# Revit family: DFM Doors - double leaf door EI 120
name_source: partatom
category: Doors
revit_build: Autodesk Revit 2017 (Build: 20190507_1515(x64)
units: mm (PartAtom-declared; Revit-internal decimal feet)

## family parameters
Always vertical = Yes
Cut with Voids When Loaded = No
Host = Wall
OmniClass Number = 23.30.10.00
OmniClass Title = Doors
Room Calculation Point = Yes
Shared = No

## types (1)
- 2018x1840 internal frame
    Clear opening height = 2018 mm  [stored 6.62073 ft]
    Clear opening height. Limiting dimensions = ok
    Clear opening width = 1840 mm  [stored 6.03675 ft]
    Clear opening width at opened active leaf = 870.5 mm  [stored 2.85597 ft]
    Clear opening width. Limiting dimensions = ok
    Corner frame = No
    Embracing frame = No
    Fire Rating = EI 120
    Frame to frame width = 1851 mm  [stored 6.07283 ft]
    Function = Interior
    Height = 2101 mm  [stored 6.89304 ft]
    Height of the door leaf = 2050 mm  [stored 6.72572 ft]
    Internal frame = Yes
    Manufacturer = DFM Doors sp. z o. o.
    Material of astragal profie = DFM Doors - aluminium
    Material of door closer = DFM Doors - aluminium
    Material of door frame = DFM Doors - zinc coated steel
    Material of door leaf = DFM Doors - zinc coated steel
    Material of drip cap = DFM Doors - zinc coated steel
    Material of glass = DFM Doors - glazing
    Material of glass framing = DFM Doors - zinc coated steel
    Material of hinges = DFM Doors - stainless steel
    Material of ironmongery = DFM Doors - aluminium
    Model = DFM DS 120 - 2
    Offset of the active leaf axis = 523.75 mm
    Offset of the door leaf = 58 mm  [stored 0.190289 ft]
    Offset of the inter-leaf axis = 1008.5 mm  [stored 3.30873 ft]
    Offset of the passive leaf axis = 523.75 mm
    Rough Height = 2101 mm  [stored 6.89304 ft]
    Rough Width = 2017 mm  [stored 6.61745 ft]
    Thickness = 65 mm  [stored 0.213255 ft]
    Type of frame = 2
    URL = https://www.dfm-europe.eu
    Wall Closure = By host
    Width = 2017 mm  [stored 6.61745 ft]
    Width of active leaf = 963.5 mm  [stored 3.16109 ft]
    Width of passive leaf = 963.5 mm  [stored 3.16109 ft]

note: [stored X ft] marks values corroborated as IEEE doubles in the binary element streams (Revit-internal decimal feet)
